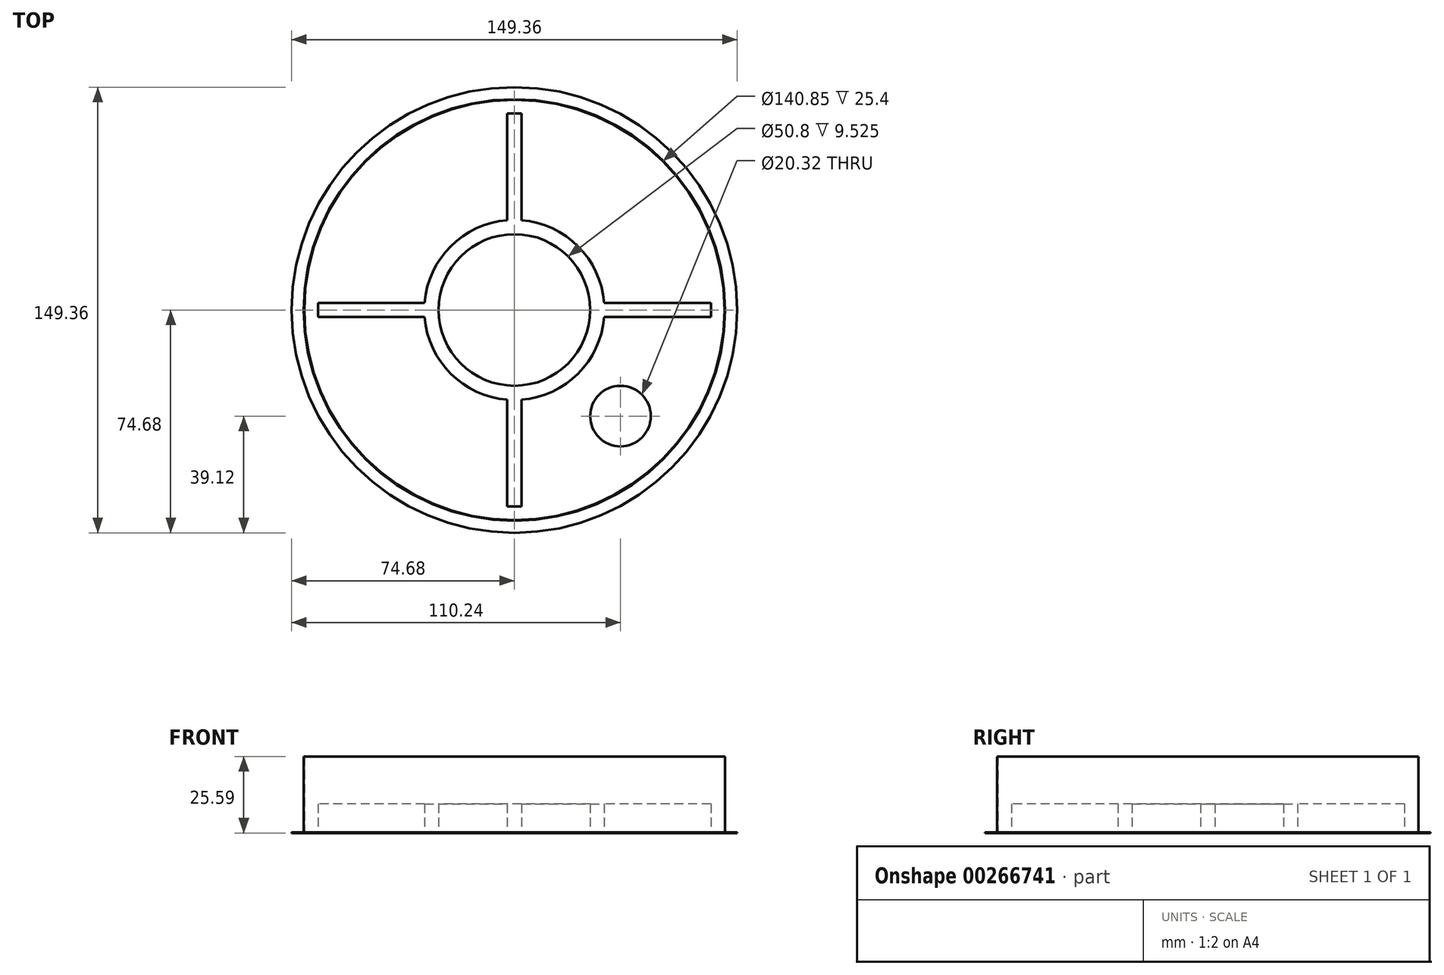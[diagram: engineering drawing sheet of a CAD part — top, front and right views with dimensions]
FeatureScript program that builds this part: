
annotation { "Feature Type Name" : "Feature", "Feature Type Description" : "" }
export const myFeature = defineFeature(function(context is Context, id is Id, definition is map)
    precondition{}
    {
        {
            assignVariable(context, id + "F0", {"name" : "thk", "anyValue" : 0.19});
        }
        {
            var Q0;
            Q0=qCreatedBy(makeId("Top.planeOp"),FACE);
            var sketch = newSketch(context, id + "F1", { "sketchPlane" : qUnion([Q0])});
            skCircle(sketch, "E0", {"center": v(0, 0) * mm, "radius": 74.68 * mm});
            skCircle(sketch, "E1", {"center": v(0, 0) * mm, "radius": 70.61 * mm});
            skSolve(sketch);
        }
        {
            var Q0;
            Q0=makeQuery(id+"F1.imprint","IMPRINT",FACE,{"disambiguationData":[TD([[makeQuery(id+"F1.imprint","IMPRINT",EDGE,{"derivedFrom":sQuery(id+"F1.wireOp",EDGE,"E0")}),1.0]])]});
            var Q1;
            Q1=makeQuery(id+"F1.imprint","IMPRINT",FACE,{"disambiguationData":[TD([[makeQuery(id+"F1.imprint","IMPRINT",EDGE,{"derivedFrom":sQuery(id+"F1.wireOp",EDGE,"E1")}),1.0]])]});
            extrude(context, id + "F2", {"entities" : qUnion([Q0, Q1]), "flatOperationType" : FlatOperationType.REMOVE, "oppositeDirection" : true, "offsetDistance" : 25.4 * mm, "depth" : (getVariable(context, 'thk')) * mm, "domain" : OperationDomain.MODEL});
        }
        {
            var Q0;
            Q0=makeQuery(id+"F1.imprint","IMPRINT",FACE,{"disambiguationData":[TD([[makeQuery(id+"F1.imprint","IMPRINT",EDGE,{"derivedFrom":sQuery(id+"F1.wireOp",EDGE,"E1")}),1.0]])]});
            extrude(context, id + "F3", {"entities" : qUnion([Q0]), "operationType" : NewBodyOperationType.ADD, "flatOperationType" : FlatOperationType.REMOVE, "offsetDistance" : 25.4 * mm, "depth" : 25.4 * mm, "domain" : OperationDomain.MODEL});
        }
        {
            var Q0;
            Q0=makeQuery(id+"F3.opExtrude","CAP_FACE",FACE,{"disambiguationData":[OSD([sQuery(id+"F1.wireOp",EDGE,"E1")])],"isStart":false});
            shell(context, id + "F4", {"entities" : qUnion([Q0]), "thickness" : (getVariable(context, 'thk')) * mm});
        }
        {
            var Q0;
            Q0=makeQuery(id+"F1.imprint","IMPRINT",FACE,{"disambiguationData":[TD([[makeQuery(id+"F1.imprint","IMPRINT",EDGE,{"derivedFrom":sQuery(id+"F1.wireOp",EDGE,"E1")}),1.0]])]});
            var sketch = newSketch(context, id + "F5", { "sketchPlane" : qUnion([Q0])});
            skLineSegment(sketch, "E2.bottom", {"start": v(65.84, 2.39) * mm, "end": v(30.08, 2.39) * mm});
            skLineSegment(sketch, "E2.top", {"start": v(65.84, -2.39) * mm, "end": v(30.08, -2.39) * mm});
            skLineSegment(sketch, "E2.left", {"start": v(65.84, 2.39) * mm, "end": v(65.84, -2.39) * mm});
            skLineSegment(sketch, "E2.right", {"start": v(-65.84, 2.39) * mm, "end": v(-65.84, -2.39) * mm});
            skPoint(sketch, "E2.middle", {"position": v(0, 0) * mm});
            skLineSegment(sketch, "E3.bottom", {"start": v(2.39, 65.84) * mm, "end": v(-2.39, 65.84) * mm});
            skLineSegment(sketch, "E3.top", {"start": v(2.39, -65.84) * mm, "end": v(-2.39, -65.84) * mm});
            skLineSegment(sketch, "E3.left", {"start": v(2.39, 65.84) * mm, "end": v(2.39, 30.08) * mm});
            skLineSegment(sketch, "E3.right", {"start": v(-2.39, 65.84) * mm, "end": v(-2.39, 30.08) * mm});
            skCircle(sketch, "E4", {"center": v(0, 0) * mm, "radius": 25.4 * mm});
            skArc(sketch, "E5.0", {"start": v(-2.39, 30.08) * mm, "mid": v(-21.34, 21.34) * mm, "end": v(-30.08, 2.39) * mm});
            skLineSegment(sketch, "E6.trimOffspring", {"start": v(-30.08, 2.39) * mm, "end": v(-65.84, 2.39) * mm});
            skArc(sketch, "E7.trimOffspring", {"start": v(-30.08, -2.39) * mm, "mid": v(-21.34, -21.34) * mm, "end": v(-2.39, -30.08) * mm});
            skLineSegment(sketch, "E8.trimOffspring", {"start": v(-30.08, -2.39) * mm, "end": v(-65.84, -2.39) * mm});
            skLineSegment(sketch, "E9.trimOffspring", {"start": v(-2.39, -30.08) * mm, "end": v(-2.39, -65.84) * mm});
            skArc(sketch, "E10.trimOffspring", {"start": v(2.39, -30.08) * mm, "mid": v(21.34, -21.34) * mm, "end": v(30.08, -2.39) * mm});
            skLineSegment(sketch, "E11.trimOffspring", {"start": v(2.39, -30.08) * mm, "end": v(2.39, -65.84) * mm});
            skArc(sketch, "E12.trimOffspring", {"start": v(30.08, 2.39) * mm, "mid": v(21.34, 21.34) * mm, "end": v(2.39, 30.08) * mm});
            skSolve(sketch);
        }
        {
            var Q0;
            Q0=makeQuery(id+"F5.imprint","IMPRINT",FACE,{"disambiguationData":[TD([[makeQuery(id+"F5.imprint","IMPRINT",EDGE,{"derivedFrom":sQuery(id+"F5.wireOp",EDGE,"E2.bottom")}),1.0]])]});
            extrude(context, id + "F6", {"entities" : qUnion([Q0]), "operationType" : NewBodyOperationType.ADD, "depth" : 9.52 * mm});
        }
        {
            var Q0;
            Q0=makeQuery(id+"F1.imprint","IMPRINT",FACE,{"disambiguationData":[TD([[makeQuery(id+"F1.imprint","IMPRINT",EDGE,{"derivedFrom":sQuery(id+"F1.wireOp",EDGE,"E1")}),1.0]])]});
            var sketch = newSketch(context, id + "F7", { "sketchPlane" : qUnion([Q0])});
            skCircle(sketch, "E13", {"center": v(35.56, -35.56) * mm, "radius": 10.16 * mm});
            skSolve(sketch);
        }
        {
            var Q0;
            Q0=makeQuery(id+"F7.imprint","IMPRINT",FACE,{"disambiguationData":[TD([[makeQuery(id+"F7.imprint","IMPRINT",EDGE,{"derivedFrom":sQuery(id+"F7.wireOp",EDGE,"E13")}),1.0]])]});
            extrude(context, id + "F8", {"entities" : qUnion([Q0]), "operationType" : NewBodyOperationType.REMOVE, "oppositeDirection" : true, "depth" : 25.4 * mm});
        }
    });
